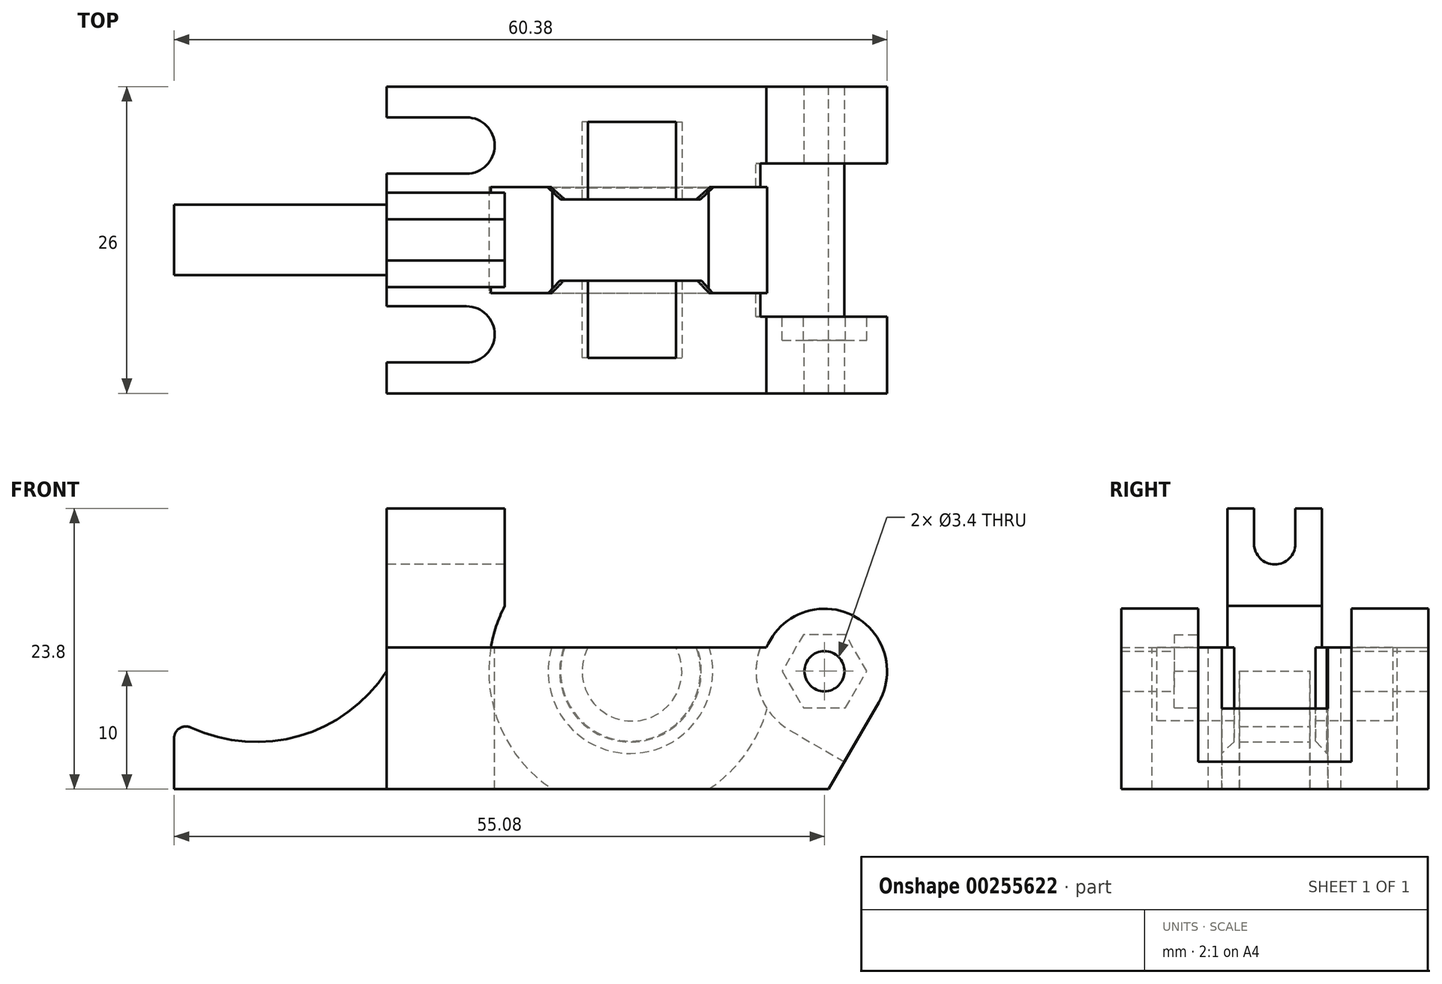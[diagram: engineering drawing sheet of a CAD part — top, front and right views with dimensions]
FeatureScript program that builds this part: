
annotation { "Feature Type Name" : "Feature", "Feature Type Description" : "" }
export const myFeature = defineFeature(function(context is Context, id is Id, definition is map)
    precondition{}
    {
        {
            var Q0;
            Q0=qCreatedBy(makeId("Front.planeOp"),FACE);
            var sketch = newSketch(context, id + "F0", { "sketchPlane" : qUnion([Q0])});
            skLineSegment(sketch, "E0.bottom", {"start": v(-37.08, -10) * mm, "end": v(0.35, -10) * mm});
            skLineSegment(sketch, "E0.top", {"start": v(-37.08, 2) * mm, "end": v(-4.9, 2) * mm});
            skLineSegment(sketch, "E0.left", {"start": v(-37.08, -10) * mm, "end": v(-37.08, 2) * mm});
            skArc(sketch, "E1", {"start": v(4.59, -2.65) * mm, "mid": v(2.33, 4.76) * mm, "end": v(-4.9, 2) * mm});
            skCircle(sketch, "E2", {"center": v(0, 0) * mm, "radius": 1.7 * mm});
            skLineSegment(sketch, "E3", {"start": v(4.59, -2.65) * mm, "end": v(0.35, -10) * mm});
            skSolve(sketch);
        }
        {
            var Q0;
            Q0=makeQuery(id+"F0.imprint","IMPRINT",FACE,{"disambiguationData":[TD([[makeQuery(id+"F0.imprint","IMPRINT",EDGE,{"derivedFrom":sQuery(id+"F0.wireOp",EDGE,"E0.bottom")}),1.0]])]});
            extrude(context, id + "F1", {"entities" : qUnion([Q0]), "endBound" : BoundingType.SYMMETRIC, "depth" : 26 * mm});
        }
        {
            var Q0;
            Q0=makeQuery(id+"F1.opExtrude","SWEPT_FACE",FACE,{"disambiguationData":[OSD([sQuery(id+"F0.wireOp",EDGE,"E0.top")])]});
            var sketch = newSketch(context, id + "F2", { "sketchPlane" : qUnion([Q0])});
            skLineSegment(sketch, "E4.bottom", {"start": v(-37.08, 10.38) * mm, "end": v(-30.3, 10.38) * mm});
            skLineSegment(sketch, "E4.top", {"start": v(-37.08, 5.62) * mm, "end": v(-30.3, 5.62) * mm});
            skLineSegment(sketch, "E4.left", {"start": v(-37.08, 10.38) * mm, "end": v(-37.08, 5.62) * mm});
            skArc(sketch, "E5", {"start": v(-30.3, 5.62) * mm, "mid": v(-27.93, 8) * mm, "end": v(-30.3, 10.38) * mm});
            skArc(sketch, "E6.MirrorCS", {"start": v(-30.3, -5.62) * mm, "mid": v(-27.93, -8) * mm, "end": v(-30.3, -10.38) * mm});
            skLineSegment(sketch, "E7.MirrorCS", {"start": v(-37.08, -10.38) * mm, "end": v(-37.08, -5.62) * mm});
            skLineSegment(sketch, "E8.MirrorCS", {"start": v(-37.08, -10.38) * mm, "end": v(-30.3, -10.38) * mm});
            skLineSegment(sketch, "E9.MirrorCS", {"start": v(-37.08, -5.62) * mm, "end": v(-30.3, -5.62) * mm});
            skCircle(sketch, "E10", {"center": v(-30.3, 8) * mm, "radius": 5.02 * mm, "construction": true});
            skCircle(sketch, "E11", {"center": v(-30.3, -8) * mm, "radius": 5.02 * mm, "construction": true});
            skSolve(sketch);
        }
        {
            var Q0;
            Q0 = qSketchRegion(id + "F2", true);
            extrude(context, id + "F3", {"entities" : qUnion([Q0]), "operationType" : NewBodyOperationType.REMOVE, "endBound" : BoundingType.THROUGH_ALL, "oppositeDirection" : true, "depth" : 25 * mm});
        }
        {
            var Q0;
            Q0=qCreatedBy(makeId("Front.planeOp"),FACE);
            var sketch = newSketch(context, id + "F4", { "sketchPlane" : qUnion([Q0])});
            skArc(sketch, "E12", {"start": v(5.8, 0) * mm, "mid": v(-2.9, 5.02) * mm, "end": v(-2.9, -5.02) * mm});
            skLineSegment(sketch, "E13", {"start": v(-2.9, -5.02) * mm, "end": v(5.8, -10.05) * mm});
            skLineSegment(sketch, "E14", {"start": v(5.8, -10.05) * mm, "end": v(5.8, 0) * mm});
            skSolve(sketch);
        }
        {
            var Q0;
            Q0 = qSketchRegion(id + "F4", true);
            extrude(context, id + "F5", {"entities" : qUnion([Q0]), "operationType" : NewBodyOperationType.REMOVE, "endBound" : BoundingType.SYMMETRIC, "depth" : 13 * mm});
        }
        {
            var Q0;
            Q0=makeQuery(id+"F1.opExtrude","SWEPT_FACE",FACE,{"disambiguationData":[OSD([sQuery(id+"F0.wireOp",EDGE,"E0.top")])]});
            var sketch = newSketch(context, id + "F6", { "sketchPlane" : qUnion([Q0])});
            skLineSegment(sketch, "E15.bottom", {"start": v(-37.08, -4) * mm, "end": v(-27.08, -4) * mm});
            skLineSegment(sketch, "E15.top", {"start": v(-37.08, 4) * mm, "end": v(-27.08, 4) * mm});
            skLineSegment(sketch, "E15.left", {"start": v(-37.08, -4) * mm, "end": v(-37.08, 4) * mm});
            skLineSegment(sketch, "E15.right", {"start": v(-27.08, -4) * mm, "end": v(-27.08, 4) * mm});
            skSolve(sketch);
        }
        {
            var Q0;
            Q0 = qSketchRegion(id + "F6", true);
            extrude(context, id + "F7", {"entities" : qUnion([Q0]), "operationType" : NewBodyOperationType.ADD, "depth" : 11.8 * mm});
        }
        {
            var Q0;
            Q0=makeQuery(id+"F7.boolean.opBoolean","MERGE",FACE,{"derivedFrom":[makeQuery(id+"F3.boolean.opBoolean","SPLIT",FACE,{"disambiguationData":[TD([makeQuery(id+"F3.opExtrude","SWEPT_FACE",FACE,{"disambiguationData":[OSD([sQuery(id+"F2.wireOp",EDGE,"E4.top")])]})])],"derivedFrom":makeQuery(id+"F1.opExtrude","SWEPT_FACE",FACE,{"disambiguationData":[OSD([sQuery(id+"F0.wireOp",EDGE,"E0.left")])]})}),makeQuery(id+"F7.opExtrude","SWEPT_FACE",FACE,{"disambiguationData":[OSD([sQuery(id+"F6.wireOp",EDGE,"E15.left")])]})]});
            var sketch = newSketch(context, id + "F8", { "sketchPlane" : qUnion([Q0])});
            skLineSegment(sketch, "E16.bottom", {"start": v(-1.75, 13.8) * mm, "end": v(1.75, 13.8) * mm});
            skLineSegment(sketch, "E16.left", {"start": v(-1.75, 13.8) * mm, "end": v(-1.75, 10.8) * mm});
            skLineSegment(sketch, "E16.right", {"start": v(1.75, 13.8) * mm, "end": v(1.75, 10.8) * mm});
            skArc(sketch, "E17", {"start": v(-1.75, 10.8) * mm, "mid": v(0, 9.05) * mm, "end": v(1.75, 10.8) * mm});
            skSolve(sketch);
        }
        {
            var Q0;
            Q0 = qSketchRegion(id + "F8", true);
            extrude(context, id + "F9", {"entities" : qUnion([Q0]), "operationType" : NewBodyOperationType.REMOVE, "endBound" : BoundingType.THROUGH_ALL, "oppositeDirection" : true, "depth" : 25 * mm});
        }
        {
            var Q0;
            Q0=qCreatedBy(makeId("Front.planeOp"),FACE);
            var sketch = newSketch(context, id + "F10", { "sketchPlane" : qUnion([Q0])});
            skCircle(sketch, "E18", {"center": v(-16.3, 0) * mm, "radius": 4.22 * mm});
            skSolve(sketch);
        }
        {
            var Q0;
            Q0 = qSketchRegion(id + "F10", true);
            extrude(context, id + "F11", {"entities" : qUnion([Q0]), "operationType" : NewBodyOperationType.REMOVE, "endBound" : BoundingType.SYMMETRIC, "oppositeDirection" : true, "depth" : 20 * mm});
        }
        {
            var Q0;
            Q0=qCreatedBy(makeId("Front.planeOp"),FACE);
            var sketch = newSketch(context, id + "F12", { "sketchPlane" : qUnion([Q0])});
            skCircle(sketch, "E19", {"center": v(-16.3, 0) * mm, "radius": 7.5 * mm});
            skSolve(sketch);
        }
        {
            var Q0;
            Q0 = qSketchRegion(id + "F12", true);
            extrude(context, id + "F13", {"entities" : qUnion([Q0]), "operationType" : NewBodyOperationType.REMOVE, "endBound" : BoundingType.SYMMETRIC, "depth" : 6.9 * mm});
        }
        {
            var Q0;
            Q0=makeQuery(id+"F11.boolean.opBoolean","INTERSECT",EDGE,{"derivedFrom":[makeQuery(id+"F1.opExtrude","SWEPT_FACE",FACE,{"disambiguationData":[OSD([sQuery(id+"F0.wireOp",EDGE,"E0.top")])]}),makeQuery(id+"F11.opExtrude","CAP_FACE",FACE,{"disambiguationData":[OSD([sQuery(id+"F10.wireOp",EDGE,"E18")])],"isStart":false})]});
            cPoint(context, id + "F14", {"entities" : qUnion([Q0]), "parameter" : 0.5});
        }
        {
            var Q0;
            Q0=qCreatedBy(makeId("Right.planeOp"),FACE);
            var Q1;
            Q1 = qCreatedBy(id + "F14" ,VERTEX);
            cPlane(context, id + "F15", {"entities" : qUnion([Q0, Q1]), "cplaneType" : CPlaneType.PLANE_POINT, "offset" : 25 * mm, "width" : 150 * mm, "height" : 150 * mm});
        }
        {
            var Q0;
            Q0=qCreatedBy(makeId("Front.planeOp"),FACE);
            var sketch = newSketch(context, id + "F16", { "sketchPlane" : qUnion([Q0])});
            skCircle(sketch, "E20", {"center": v(-16.43, 0) * mm, "radius": 6.97 * mm});
            skCircle(sketch, "E21", {"center": v(-16.43, 0) * mm, "radius": 12 * mm});
            skSolve(sketch);
        }
        {
            var Q0;
            Q0=makeQuery(id+"F16.imprint","IMPRINT",FACE,{"disambiguationData":[TD([[makeQuery(id+"F16.imprint","IMPRINT",EDGE,{"derivedFrom":sQuery(id+"F16.wireOp",EDGE,"E20")}),-1.0]])]});
            extrude(context, id + "F17", {"entities" : qUnion([Q0]), "operationType" : NewBodyOperationType.REMOVE, "endBound" : BoundingType.SYMMETRIC, "oppositeDirection" : true, "depth" : 9 * mm});
        }
        {
            var Q0;
            Q0=makeQuery(id+"F17.boolean.opBoolean","INTERSECT",EDGE,{"derivedFrom":[makeQuery(id+"F13.boolean.opBoolean","COPY",FACE,{"derivedFrom":makeQuery(id+"F13.opExtrude","CAP_FACE",FACE,{"disambiguationData":[OSD([sQuery(id+"F12.wireOp",EDGE,"E19")])],"isStart":false})}),makeQuery(id+"F17.opExtrude","SWEPT_FACE",FACE,{"disambiguationData":[OSD([sQuery(id+"F16.wireOp",EDGE,"E20")])]})]});
            var Q1;
            Q1=makeQuery(id+"F17.boolean.opBoolean","INTERSECT",EDGE,{"derivedFrom":[makeQuery(id+"F13.boolean.opBoolean","COPY",FACE,{"derivedFrom":makeQuery(id+"F13.opExtrude","CAP_FACE",FACE,{"disambiguationData":[OSD([sQuery(id+"F12.wireOp",EDGE,"E19")])],"isStart":true})}),makeQuery(id+"F17.opExtrude","SWEPT_FACE",FACE,{"disambiguationData":[OSD([sQuery(id+"F16.wireOp",EDGE,"E20")])]})]});
            chamfer(context, id + "F18", {"entities" : qUnion([Q0, Q1]), "chamferType" : ChamferType.OFFSET_ANGLE, "width" : 1.05 * mm, "oppositeDirection" : false, "angle" : 42.73 * degree, "tangentPropagation" : true});
        }
        {
            var Q0;
            Q0=qCreatedBy(makeId("Front.planeOp"),FACE);
            var sketch = newSketch(context, id + "F19", { "sketchPlane" : qUnion([Q0])});
            skLineSegment(sketch, "E22", {"start": v(-37.08, 0) * mm, "end": v(-37.08, -10) * mm});
            skLineSegment(sketch, "E23", {"start": v(-37.08, -10) * mm, "end": v(-55.08, -10) * mm});
            skLineSegment(sketch, "E24", {"start": v(-55.08, -10) * mm, "end": v(-55.08, -5.68) * mm});
            skArc(sketch, "E25", {"start": v(-53.66, -4.77) * mm, "mid": v(-44.48, -5.49) * mm, "end": v(-37.08, 0) * mm});
            skPoint(sketch, "E26.visualSharp", {"position": v(-55.08, -4) * mm});
            skArc(sketch, "E26.filletArc", {"start": v(-53.66, -4.77) * mm, "mid": v(-54.62, -4.84) * mm, "end": v(-55.08, -5.68) * mm});
            skSolve(sketch);
        }
        {
            var Q0;
            Q0 = qSketchRegion(id + "F19", true);
            extrude(context, id + "F20", {"entities" : qUnion([Q0]), "operationType" : NewBodyOperationType.ADD, "endBound" : BoundingType.SYMMETRIC, "depth" : 5.98 * mm});
        }
        {
            var Q0;
            Q0=makeQuery(id+"F5.boolean.opBoolean","COPY",FACE,{"derivedFrom":makeQuery(id+"F5.opExtrude","CAP_FACE",FACE,{"disambiguationData":[OSD([sQuery(id+"F4.wireOp",EDGE,"E12"),sQuery(id+"F4.wireOp",EDGE,"E13"),sQuery(id+"F4.wireOp",EDGE,"E14")])],"isStart":false})});
            var sketch = newSketch(context, id + "F21", { "sketchPlane" : qUnion([Q0])});
            skCircle(sketch, "E27.cCircle", {"center": v(0, 0) * mm, "radius": 3.1 * mm, "construction": true});
            skLineSegment(sketch, "E27.0", {"start": v(-1.79, -3.1) * mm, "end": v(-3.58, 0) * mm});
            skLineSegment(sketch, "E27.1", {"start": v(-3.58, 0) * mm, "end": v(-1.79, 3.1) * mm});
            skLineSegment(sketch, "E27.2", {"start": v(-1.79, 3.1) * mm, "end": v(1.79, 3.1) * mm});
            skLineSegment(sketch, "E27.3", {"start": v(1.79, 3.1) * mm, "end": v(3.58, 0) * mm});
            skLineSegment(sketch, "E27.4", {"start": v(3.58, 0) * mm, "end": v(1.79, -3.1) * mm});
            skLineSegment(sketch, "E27.5", {"start": v(1.79, -3.1) * mm, "end": v(-1.79, -3.1) * mm});
            skPoint(sketch, "E27.0.midPoint", {"position": v(-2.68, -1.55) * mm});
            skSolve(sketch);
        }
        {
            var Q0;
            Q0 = qSketchRegion(id + "F21", true);
            extrude(context, id + "F22", {"entities" : qUnion([Q0]), "operationType" : NewBodyOperationType.REMOVE, "oppositeDirection" : true, "depth" : 2 * mm});
        }
    });
